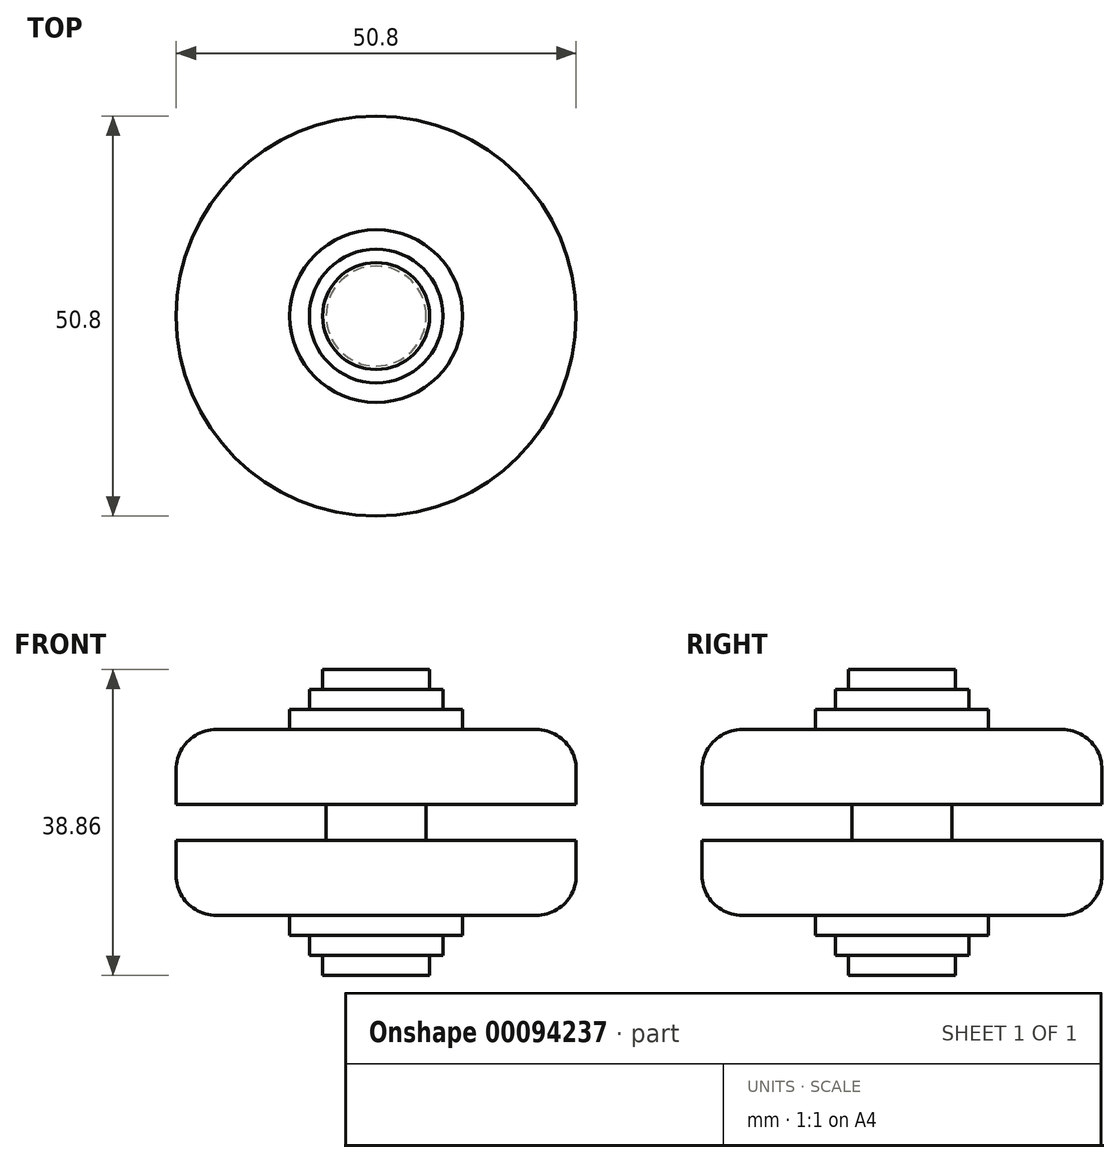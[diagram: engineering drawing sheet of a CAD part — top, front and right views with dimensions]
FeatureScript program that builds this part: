
annotation { "Feature Type Name" : "Feature", "Feature Type Description" : "" }
export const myFeature = defineFeature(function(context is Context, id is Id, definition is map)
    precondition{}
    {
        {
            var Q0;
            Q0=qCreatedBy(makeId("Top.planeOp"),FACE);
            var sketch = newSketch(context, id + "F0", { "sketchPlane" : qUnion([Q0])});
            skCircle(sketch, "E0", {"center": v(0, 0) * mm, "radius": 25.4 * mm});
            skSolve(sketch);
        }
        {
            var Q0;
            Q0 = qSketchRegion(id + "F0", true);
            extrude(context, id + "F1", {"entities" : qUnion([Q0]), "depth" : 9.52 * mm});
        }
        {
            var Q0;
            Q0=makeQuery(id+"F1.opExtrude","CAP_FACE",FACE,{"disambiguationData":[OSD([sQuery(id+"F0.wireOp",EDGE,"E0")])],"isStart":false});
            var sketch = newSketch(context, id + "F2", { "sketchPlane" : qUnion([Q0])});
            skCircle(sketch, "E1", {"center": v(0, 0) * mm, "radius": 6.35 * mm});
            skSolve(sketch);
        }
        {
            var Q0;
            Q0 = qSketchRegion(id + "F2", true);
            extrude(context, id + "F3", {"entities" : qUnion([Q0]), "operationType" : NewBodyOperationType.ADD, "depth" : 4.57 * mm});
        }
        {
            var Q0;
            Q0=makeQuery(id+"F3.opExtrude","CAP_FACE",FACE,{"disambiguationData":[OSD([sQuery(id+"F2.wireOp",EDGE,"E1")])],"isStart":false});
            var sketch = newSketch(context, id + "F4", { "sketchPlane" : qUnion([Q0])});
            skCircle(sketch, "E2", {"center": v(0, 0) * mm, "radius": 25.4 * mm});
            skSolve(sketch);
        }
        {
            var Q0;
            Q0=makeQuery(id+"F0.imprint","IMPRINT",FACE,{"disambiguationData":[TD([[makeQuery(id+"F0.imprint","IMPRINT",EDGE,{"derivedFrom":sQuery(id+"F0.wireOp",EDGE,"E0")}),1.0]])]});
            var Q1;
            Q1=makeQuery(id+"F4.imprint","IMPRINT",FACE,{"disambiguationData":[TD([[makeQuery(id+"F4.imprint","IMPRINT",EDGE,{"derivedFrom":sQuery(id+"F4.wireOp",EDGE,"E2")}),1.0]])]});
            var Q2;
            Q2=makeQuery(id+"F4.imprint","IMPRINT",FACE,{"disambiguationData":[TD([[makeQuery(id+"F4.imprint","IMPRINT",EDGE,{"derivedFrom":makeQuery(id+"F3.opExtrude","CAP_EDGE",EDGE,{"disambiguationData":[OSD([sQuery(id+"F2.wireOp",EDGE,"E1")])],"isStart":false})}),1.0]])]});
            extrude(context, id + "F5", {"entities" : qUnion([Q0, Q1, Q2]), "operationType" : NewBodyOperationType.ADD, "depth" : 9.52 * mm});
        }
        {
            var Q0;
            Q0=makeQuery(id+"F5.opExtrude","CAP_FACE",FACE,{"disambiguationData":[OSD([sQuery(id+"F4.wireOp",EDGE,"E2")])],"isStart":false});
            var Q1;
            Q1=makeQuery(id+"F1.opExtrude","CAP_FACE",FACE,{"disambiguationData":[OSD([sQuery(id+"F0.wireOp",EDGE,"E0")])],"isStart":true});
            fillet(context, id + "F6", {"entities" : qUnion([Q0, Q1]), "radius" : 5.08 * mm, "tangentPropagation" : true, "allowEdgeOverflow" : false});
        }
        {
            var Q0;
            Q0=makeQuery(id+"F5.opExtrude","CAP_FACE",FACE,{"disambiguationData":[OSD([sQuery(id+"F4.wireOp",EDGE,"E2")])],"isStart":false});
            var sketch = newSketch(context, id + "F7", { "sketchPlane" : qUnion([Q0])});
            skCircle(sketch, "E3", {"center": v(0, 0) * mm, "radius": 10.98 * mm});
            skSolve(sketch);
        }
        {
            var Q0;
            Q0=makeQuery(id+"F7.imprint","IMPRINT",FACE,{"disambiguationData":[TD([[makeQuery(id+"F7.imprint","IMPRINT",EDGE,{"derivedFrom":sQuery(id+"F7.wireOp",EDGE,"E3")}),1.0]])]});
            extrude(context, id + "F8", {"entities" : qUnion([Q0]), "operationType" : NewBodyOperationType.ADD, "depth" : 2.54 * mm});
        }
        {
            var Q0;
            Q0=makeQuery(id+"F8.opExtrude","CAP_FACE",FACE,{"disambiguationData":[OSD([sQuery(id+"F7.wireOp",EDGE,"E3")])],"isStart":false});
            var sketch = newSketch(context, id + "F9", { "sketchPlane" : qUnion([Q0])});
            skCircle(sketch, "E4", {"center": v(0, 0) * mm, "radius": 8.49 * mm});
            skSolve(sketch);
        }
        {
            var Q0;
            Q0 = qSketchRegion(id + "F9", true);
            extrude(context, id + "F10", {"entities" : qUnion([Q0]), "operationType" : NewBodyOperationType.ADD, "depth" : 2.54 * mm});
        }
        {
            var Q0;
            Q0=makeQuery(id+"F10.opExtrude","CAP_FACE",FACE,{"disambiguationData":[OSD([sQuery(id+"F9.wireOp",EDGE,"E4")])],"isStart":false});
            var sketch = newSketch(context, id + "F11", { "sketchPlane" : qUnion([Q0])});
            skCircle(sketch, "E5", {"center": v(0, 0) * mm, "radius": 6.8 * mm});
            skSolve(sketch);
        }
        {
            var Q0;
            Q0 = qSketchRegion(id + "F11", true);
            extrude(context, id + "F12", {"entities" : qUnion([Q0]), "operationType" : NewBodyOperationType.ADD, "depth" : 2.54 * mm});
        }
        {
            var Q0;
            Q0=makeQuery(id+"F1.opExtrude","CAP_FACE",FACE,{"disambiguationData":[OSD([sQuery(id+"F0.wireOp",EDGE,"E0")])],"isStart":true});
            var sketch = newSketch(context, id + "F13", { "sketchPlane" : qUnion([Q0])});
            skCircle(sketch, "E6", {"center": v(0, 0) * mm, "radius": 10.98 * mm});
            skSolve(sketch);
        }
        {
            var Q0;
            Q0 = qSketchRegion(id + "F13", true);
            var Q1;
            Q1=makeQuery(id+"F10.opExtrude","CAP_FACE",FACE,{"disambiguationData":[OSD([sQuery(id+"F9.wireOp",EDGE,"E4")])],"isStart":false});
            extrude(context, id + "F14", {"entities" : qUnion([Q0, Q1]), "operationType" : NewBodyOperationType.ADD, "depth" : 2.54 * mm});
        }
        {
            var Q0;
            Q0=makeQuery(id+"F14.opExtrude","CAP_FACE",FACE,{"disambiguationData":[OSD([sQuery(id+"F13.wireOp",EDGE,"E6")])],"isStart":false});
            var sketch = newSketch(context, id + "F15", { "sketchPlane" : qUnion([Q0])});
            skCircle(sketch, "E7", {"center": v(0, 0) * mm, "radius": 8.48 * mm});
            skSolve(sketch);
        }
        {
            var Q0;
            Q0 = qSketchRegion(id + "F15", true);
            extrude(context, id + "F16", {"entities" : qUnion([Q0]), "operationType" : NewBodyOperationType.ADD, "depth" : 2.54 * mm});
        }
        {
            var Q0;
            Q0=makeQuery(id+"F16.opExtrude","CAP_FACE",FACE,{"disambiguationData":[OSD([sQuery(id+"F15.wireOp",EDGE,"E7")])],"isStart":false});
            var sketch = newSketch(context, id + "F17", { "sketchPlane" : qUnion([Q0])});
            skCircle(sketch, "E8", {"center": v(0, 0) * mm, "radius": 6.8 * mm});
            skSolve(sketch);
        }
        {
            var Q0;
            Q0 = qSketchRegion(id + "F17", true);
            extrude(context, id + "F18", {"entities" : qUnion([Q0]), "operationType" : NewBodyOperationType.ADD, "depth" : 2.54 * mm});
        }
    });
